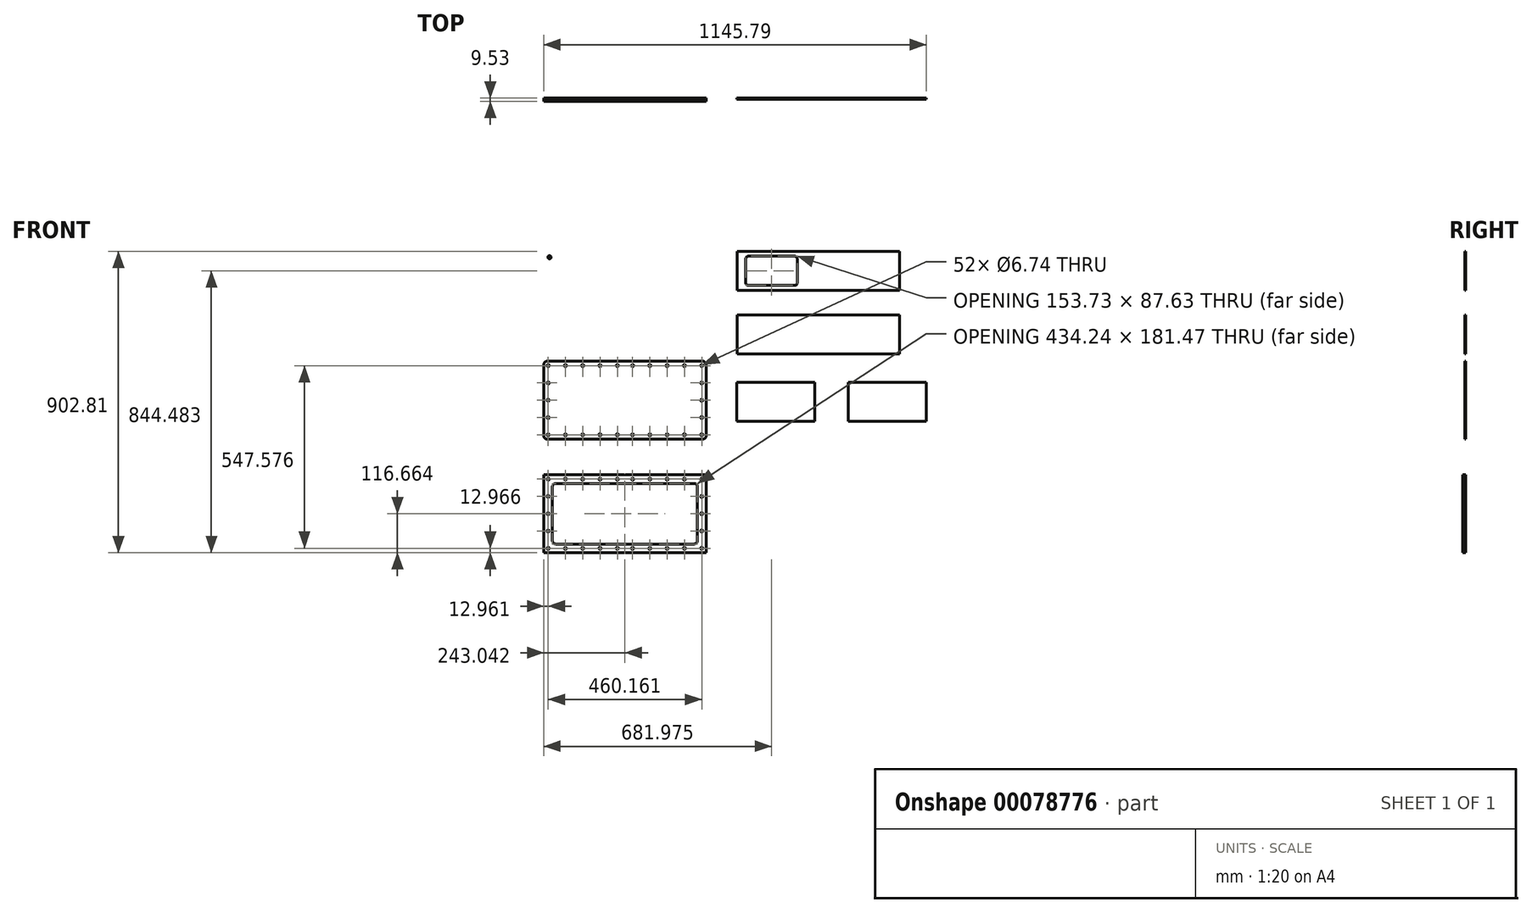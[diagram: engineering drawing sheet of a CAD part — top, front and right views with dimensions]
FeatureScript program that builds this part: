
annotation { "Feature Type Name" : "Feature", "Feature Type Description" : "" }
export const myFeature = defineFeature(function(context is Context, id is Id, definition is map)
    precondition{}
    {
        {
            var Q0;
            Q0=qCreatedBy(makeId("Front.planeOp"),FACE);
            var sketch = newSketch(context, id + "F0", { "sketchPlane" : qUnion([Q0])});
            skLineSegment(sketch, "E0", {"start": v(7.41, 48.73) * mm, "end": v(240.74, 48.73) * mm});
            skLineSegment(sketch, "E1", {"start": v(7.41, 48.73) * mm, "end": v(7.41, -67.93) * mm});
            skLineSegment(sketch, "E2", {"start": v(7.41, -67.93) * mm, "end": v(240.74, -67.93) * mm});
            skLineSegment(sketch, "E3", {"start": v(341.56, 48.73) * mm, "end": v(574.88, 48.73) * mm});
            skLineSegment(sketch, "E4", {"start": v(341.56, -67.93) * mm, "end": v(574.88, -67.93) * mm});
            skLineSegment(sketch, "E5", {"start": v(341.56, 48.73) * mm, "end": v(341.56, -67.93) * mm});
            skLineSegment(sketch, "E6", {"start": v(8.27, 250.62) * mm, "end": v(494.36, 250.62) * mm});
            skLineSegment(sketch, "E7", {"start": v(8.27, 133.96) * mm, "end": v(494.36, 133.96) * mm});
            skLineSegment(sketch, "E8", {"start": v(8.27, 441.5) * mm, "end": v(494.36, 441.5) * mm});
            skLineSegment(sketch, "E9", {"start": v(8.27, 324.83) * mm, "end": v(494.36, 324.83) * mm});
            skLineSegment(sketch, "E10", {"start": v(8.27, 250.62) * mm, "end": v(8.27, 133.96) * mm});
            skLineSegment(sketch, "E11", {"start": v(8.27, 441.5) * mm, "end": v(8.27, 324.83) * mm});
            skCircle(sketch, "E12", {"center": v(-553.9, 424) * mm, "radius": 4.86 * mm});
            skCircle(sketch, "E13", {"center": v(-553.9, 245.77) * mm, "radius": 4.86 * mm});
            skCircle(sketch, "E14", {"center": v(-101.84, 424) * mm, "radius": 4.86 * mm});
            skCircle(sketch, "E15", {"center": v(-131, 245.77) * mm, "radius": 4.86 * mm});
            skCircle(sketch, "E16", {"center": v(-372.43, 430.48) * mm, "radius": 4.86 * mm});
            skCircle(sketch, "E17", {"center": v(-255.77, 430.48) * mm, "radius": 4.86 * mm});
            skCircle(sketch, "E18", {"center": v(-411.31, 239.29) * mm, "radius": 4.86 * mm});
            skCircle(sketch, "E19", {"center": v(-294.65, 239.29) * mm, "radius": 4.86 * mm});
            skLineSegment(sketch, "E20", {"start": v(-570.91, 451.55) * mm, "end": v(-84.83, 451.55) * mm});
            skLineSegment(sketch, "E21", {"start": v(-570.91, 218.23) * mm, "end": v(-84.83, 218.23) * mm});
            skLineSegment(sketch, "E22", {"start": v(-84.83, 451.55) * mm, "end": v(-84.83, 218.23) * mm});
            skLineSegment(sketch, "E23", {"start": v(-570.91, 451.55) * mm, "end": v(-570.91, 218.23) * mm});
            skCircle(sketch, "E24", {"center": v(-515.01, 401.32) * mm, "radius": 4.4 * mm});
            skCircle(sketch, "E25", {"center": v(-515.01, 268.45) * mm, "radius": 4.4 * mm});
            skCircle(sketch, "E26", {"center": v(-369.83, 401.32) * mm, "radius": 4.4 * mm});
            skCircle(sketch, "E27", {"center": v(-369.83, 268.45) * mm, "radius": 4.4 * mm});
            skCircle(sketch, "E28", {"center": v(-285.9, 401.32) * mm, "radius": 4.4 * mm});
            skCircle(sketch, "E29", {"center": v(-285.9, 268.45) * mm, "radius": 4.4 * mm});
            skCircle(sketch, "E30", {"center": v(-140.73, 401.32) * mm, "radius": 4.4 * mm});
            skCircle(sketch, "E31", {"center": v(-140.73, 268.45) * mm, "radius": 4.4 * mm});
            skLineSegment(sketch, "E32", {"start": v(-492.98, 385.76) * mm, "end": v(-391.87, 385.76) * mm});
            skLineSegment(sketch, "E33", {"start": v(-499.46, 290.49) * mm, "end": v(-499.46, 379.28) * mm});
            skLineSegment(sketch, "E34", {"start": v(-492.98, 284) * mm, "end": v(-391.87, 284) * mm});
            skLineSegment(sketch, "E35", {"start": v(-385.39, 290.49) * mm, "end": v(-385.39, 379.28) * mm});
            skLineSegment(sketch, "E36", {"start": v(-270.35, 379.28) * mm, "end": v(-270.35, 290.49) * mm});
            skLineSegment(sketch, "E37", {"start": v(-156.28, 379.28) * mm, "end": v(-156.28, 290.49) * mm});
            skArc(sketch, "E38", {"start": v(-492.98, 385.76) * mm, "mid": v(-497.56, 383.86) * mm, "end": v(-499.46, 379.28) * mm});
            skLineSegment(sketch, "E39", {"start": v(-263.87, 385.76) * mm, "end": v(-162.76, 385.76) * mm});
            skLineSegment(sketch, "E40", {"start": v(-263.87, 284) * mm, "end": v(-162.76, 284) * mm});
            skArc(sketch, "E41", {"start": v(-385.39, 379.28) * mm, "mid": v(-387.29, 383.86) * mm, "end": v(-391.87, 385.76) * mm});
            skArc(sketch, "E42", {"start": v(-391.87, 284) * mm, "mid": v(-387.29, 285.9) * mm, "end": v(-385.39, 290.49) * mm});
            skArc(sketch, "E43", {"start": v(-499.46, 290.49) * mm, "mid": v(-497.56, 285.9) * mm, "end": v(-492.98, 284) * mm});
            skArc(sketch, "E44", {"start": v(-270.35, 290.49) * mm, "mid": v(-268.45, 285.9) * mm, "end": v(-263.87, 284) * mm});
            skArc(sketch, "E45", {"start": v(-263.87, 385.76) * mm, "mid": v(-268.45, 383.86) * mm, "end": v(-270.35, 379.28) * mm});
            skArc(sketch, "E46", {"start": v(-156.28, 379.28) * mm, "mid": v(-158.18, 383.86) * mm, "end": v(-162.76, 385.76) * mm});
            skArc(sketch, "E47", {"start": v(-162.76, 284) * mm, "mid": v(-158.18, 285.9) * mm, "end": v(-156.28, 290.49) * mm});
            skLineSegment(sketch, "E48", {"start": v(-561.19, -121.14) * mm, "end": v(-94.55, -121.14) * mm});
            skLineSegment(sketch, "E49", {"start": v(-561.19, 112.18) * mm, "end": v(-94.55, 112.18) * mm});
            skLineSegment(sketch, "E50", {"start": v(-570.91, 102.46) * mm, "end": v(-570.91, -111.42) * mm});
            skLineSegment(sketch, "E51", {"start": v(-84.83, 102.46) * mm, "end": v(-84.83, -111.42) * mm});
            skCircle(sketch, "E52", {"center": v(-557.95, 99.22) * mm, "radius": 3.37 * mm});
            skCircle(sketch, "E53", {"center": v(-506.1, 99.22) * mm, "radius": 3.37 * mm});
            skCircle(sketch, "E54", {"center": v(-454.25, 99.22) * mm, "radius": 3.37 * mm});
            skCircle(sketch, "E55", {"center": v(-402.4, 99.22) * mm, "radius": 3.37 * mm});
            skCircle(sketch, "E56", {"center": v(-350.55, 99.22) * mm, "radius": 3.37 * mm});
            skCircle(sketch, "E57", {"center": v(-305.18, 99.22) * mm, "radius": 3.37 * mm});
            skCircle(sketch, "E58", {"center": v(-253.33, 99.22) * mm, "radius": 3.37 * mm});
            skCircle(sketch, "E59", {"center": v(-201.49, 99.22) * mm, "radius": 3.37 * mm});
            skCircle(sketch, "E60", {"center": v(-149.64, 99.22) * mm, "radius": 3.37 * mm});
            skCircle(sketch, "E61", {"center": v(-97.79, 99.22) * mm, "radius": 3.37 * mm});
            skCircle(sketch, "E62", {"center": v(-97.79, 47.37) * mm, "radius": 3.37 * mm});
            skCircle(sketch, "E63", {"center": v(-97.79, -4.48) * mm, "radius": 3.37 * mm});
            skCircle(sketch, "E64", {"center": v(-97.79, -56.33) * mm, "radius": 3.37 * mm});
            skCircle(sketch, "E65", {"center": v(-97.79, -108.17) * mm, "radius": 3.37 * mm});
            skCircle(sketch, "E66", {"center": v(-149.64, -108.17) * mm, "radius": 3.37 * mm});
            skCircle(sketch, "E67", {"center": v(-201.49, -108.17) * mm, "radius": 3.37 * mm});
            skCircle(sketch, "E68", {"center": v(-253.33, -108.17) * mm, "radius": 3.37 * mm});
            skCircle(sketch, "E69", {"center": v(-305.18, -108.17) * mm, "radius": 3.37 * mm});
            skCircle(sketch, "E70", {"center": v(-350.55, -108.17) * mm, "radius": 3.37 * mm});
            skCircle(sketch, "E71", {"center": v(-402.4, -108.17) * mm, "radius": 3.37 * mm});
            skCircle(sketch, "E72", {"center": v(-454.25, -108.17) * mm, "radius": 3.37 * mm});
            skCircle(sketch, "E73", {"center": v(-506.1, -108.17) * mm, "radius": 3.37 * mm});
            skCircle(sketch, "E74", {"center": v(-557.95, -108.17) * mm, "radius": 3.37 * mm});
            skCircle(sketch, "E75", {"center": v(-557.95, -56.33) * mm, "radius": 3.37 * mm});
            skCircle(sketch, "E76", {"center": v(-557.95, -4.48) * mm, "radius": 3.37 * mm});
            skCircle(sketch, "E77", {"center": v(-557.95, 47.37) * mm, "radius": 3.37 * mm});
            skArc(sketch, "E78", {"start": v(-84.83, 102.46) * mm, "mid": v(-87.67, 109.34) * mm, "end": v(-94.55, 112.18) * mm});
            skArc(sketch, "E79", {"start": v(-94.55, -121.14) * mm, "mid": v(-87.67, -118.29) * mm, "end": v(-84.83, -111.42) * mm});
            skArc(sketch, "E80", {"start": v(-570.91, -111.42) * mm, "mid": v(-568.06, -118.29) * mm, "end": v(-561.19, -121.14) * mm});
            skArc(sketch, "E81", {"start": v(-561.19, 112.18) * mm, "mid": v(-568.06, 109.34) * mm, "end": v(-570.91, 102.46) * mm});
            skLineSegment(sketch, "E82", {"start": v(-570.91, -461.32) * mm, "end": v(-84.83, -461.32) * mm});
            skLineSegment(sketch, "E83", {"start": v(-570.91, -228) * mm, "end": v(-84.83, -228) * mm});
            skLineSegment(sketch, "E84", {"start": v(-570.91, -228) * mm, "end": v(-570.91, -461.32) * mm});
            skLineSegment(sketch, "E85", {"start": v(-84.83, -228) * mm, "end": v(-84.83, -461.32) * mm});
            skCircle(sketch, "E86", {"center": v(-557.95, -240.96) * mm, "radius": 3.37 * mm});
            skCircle(sketch, "E87", {"center": v(-506.1, -240.96) * mm, "radius": 3.37 * mm});
            skCircle(sketch, "E88", {"center": v(-454.25, -240.96) * mm, "radius": 3.37 * mm});
            skCircle(sketch, "E89", {"center": v(-402.4, -240.96) * mm, "radius": 3.37 * mm});
            skCircle(sketch, "E90", {"center": v(-350.55, -240.96) * mm, "radius": 3.37 * mm});
            skCircle(sketch, "E91", {"center": v(-305.18, -240.96) * mm, "radius": 3.37 * mm});
            skCircle(sketch, "E92", {"center": v(-253.33, -240.96) * mm, "radius": 3.37 * mm});
            skCircle(sketch, "E93", {"center": v(-201.49, -240.96) * mm, "radius": 3.37 * mm});
            skCircle(sketch, "E94", {"center": v(-149.64, -240.96) * mm, "radius": 3.37 * mm});
            skCircle(sketch, "E95", {"center": v(-97.79, -240.96) * mm, "radius": 3.37 * mm});
            skCircle(sketch, "E96", {"center": v(-97.79, -292.8) * mm, "radius": 3.37 * mm});
            skCircle(sketch, "E97", {"center": v(-97.79, -344.66) * mm, "radius": 3.37 * mm});
            skCircle(sketch, "E98", {"center": v(-97.79, -396.5) * mm, "radius": 3.37 * mm});
            skCircle(sketch, "E99", {"center": v(-97.79, -448.35) * mm, "radius": 3.37 * mm});
            skCircle(sketch, "E100", {"center": v(-149.64, -448.35) * mm, "radius": 3.37 * mm});
            skCircle(sketch, "E101", {"center": v(-201.49, -448.35) * mm, "radius": 3.37 * mm});
            skCircle(sketch, "E102", {"center": v(-253.33, -448.35) * mm, "radius": 3.37 * mm});
            skCircle(sketch, "E103", {"center": v(-305.18, -448.35) * mm, "radius": 3.37 * mm});
            skCircle(sketch, "E104", {"center": v(-350.55, -448.35) * mm, "radius": 3.37 * mm});
            skCircle(sketch, "E105", {"center": v(-402.4, -448.35) * mm, "radius": 3.37 * mm});
            skCircle(sketch, "E106", {"center": v(-454.25, -448.35) * mm, "radius": 3.37 * mm});
            skCircle(sketch, "E107", {"center": v(-506.1, -448.35) * mm, "radius": 3.37 * mm});
            skCircle(sketch, "E108", {"center": v(-557.95, -448.35) * mm, "radius": 3.37 * mm});
            skCircle(sketch, "E109", {"center": v(-557.95, -396.5) * mm, "radius": 3.37 * mm});
            skCircle(sketch, "E110", {"center": v(-557.95, -344.66) * mm, "radius": 3.37 * mm});
            skCircle(sketch, "E111", {"center": v(-557.95, -292.8) * mm, "radius": 3.37 * mm});
            skLineSegment(sketch, "E112", {"start": v(-535.26, -253.92) * mm, "end": v(-120.47, -253.92) * mm});
            skLineSegment(sketch, "E113", {"start": v(-535.26, -435.4) * mm, "end": v(-120.47, -435.4) * mm});
            skLineSegment(sketch, "E114", {"start": v(-544.99, -263.64) * mm, "end": v(-544.99, -425.67) * mm});
            skLineSegment(sketch, "E115", {"start": v(-110.75, -263.64) * mm, "end": v(-110.75, -425.67) * mm});
            skArc(sketch, "E116", {"start": v(-535.26, -253.92) * mm, "mid": v(-542.14, -256.77) * mm, "end": v(-544.99, -263.64) * mm});
            skArc(sketch, "E117", {"start": v(-544.99, -425.67) * mm, "mid": v(-542.14, -432.54) * mm, "end": v(-535.26, -435.4) * mm});
            skArc(sketch, "E118", {"start": v(-120.47, -435.4) * mm, "mid": v(-113.6, -432.54) * mm, "end": v(-110.75, -425.67) * mm});
            skArc(sketch, "E119", {"start": v(-110.75, -263.64) * mm, "mid": v(-113.6, -256.77) * mm, "end": v(-120.47, -253.92) * mm});
            skLineSegment(sketch, "E120", {"start": v(494.36, 441.5) * mm, "end": v(494.36, 324.83) * mm});
            skLineSegment(sketch, "E121", {"start": v(494.36, 250.62) * mm, "end": v(494.36, 133.96) * mm});
            skLineSegment(sketch, "E122", {"start": v(240.74, 48.73) * mm, "end": v(240.74, -67.93) * mm});
            skLineSegment(sketch, "E123", {"start": v(574.88, 48.73) * mm, "end": v(574.88, -67.93) * mm});
            skLineSegment(sketch, "E124", {"start": v(34.2, 420.5) * mm, "end": v(34.2, 345.83) * mm});
            skLineSegment(sketch, "E125", {"start": v(187.93, 420.5) * mm, "end": v(187.93, 345.83) * mm});
            skLineSegment(sketch, "E126", {"start": v(40.68, 339.35) * mm, "end": v(181.45, 339.35) * mm});
            skLineSegment(sketch, "E127", {"start": v(40.68, 426.98) * mm, "end": v(181.45, 426.98) * mm});
            skArc(sketch, "E128", {"start": v(40.68, 426.98) * mm, "mid": v(36.1, 425.08) * mm, "end": v(34.2, 420.5) * mm});
            skArc(sketch, "E129", {"start": v(187.93, 420.5) * mm, "mid": v(186.03, 425.08) * mm, "end": v(181.45, 426.98) * mm});
            skArc(sketch, "E130", {"start": v(181.45, 339.35) * mm, "mid": v(186.03, 341.25) * mm, "end": v(187.93, 345.83) * mm});
            skArc(sketch, "E131", {"start": v(34.2, 345.83) * mm, "mid": v(36.1, 341.25) * mm, "end": v(40.68, 339.35) * mm});
            skSolve(sketch);
        }
        {
            var Q0;
            Q0=makeQuery(id+"F0.imprint","IMPRINT",FACE,{"disambiguationData":[TD([[makeQuery(id+"F0.imprint","IMPRINT",EDGE,{"derivedFrom":sQuery(id+"F0.wireOp",EDGE,"E12")}),1.0]])]});
            var Q1;
            Q1=makeQuery(id+"F0.imprint","IMPRINT",FACE,{"disambiguationData":[TD([[makeQuery(id+"F0.imprint","IMPRINT",EDGE,{"derivedFrom":sQuery(id+"F0.wireOp",EDGE,"E8")}),-1.0]])]});
            var Q2;
            Q2=makeQuery(id+"F0.imprint","IMPRINT",FACE,{"disambiguationData":[TD([[makeQuery(id+"F0.imprint","IMPRINT",EDGE,{"derivedFrom":sQuery(id+"F0.wireOp",EDGE,"E6")}),-1.0]])]});
            var Q3;
            Q3=makeQuery(id+"F0.imprint","IMPRINT",FACE,{"disambiguationData":[TD([[makeQuery(id+"F0.imprint","IMPRINT",EDGE,{"derivedFrom":sQuery(id+"F0.wireOp",EDGE,"E3")}),-1.0]])]});
            var Q4;
            Q4=makeQuery(id+"F0.imprint","IMPRINT",FACE,{"disambiguationData":[TD([[makeQuery(id+"F0.imprint","IMPRINT",EDGE,{"derivedFrom":sQuery(id+"F0.wireOp",EDGE,"E0")}),-1.0]])]});
            var Q5;
            Q5=makeQuery(id+"F0.imprint","IMPRINT",FACE,{"disambiguationData":[TD([[makeQuery(id+"F0.imprint","IMPRINT",EDGE,{"derivedFrom":sQuery(id+"F0.wireOp",EDGE,"E48")}),1.0]])]});
            extrude(context, id + "F1", {"entities" : qUnion([Q0, Q1, Q2, Q3, Q4, Q5]), "depth" : 3.17 * mm});
        }
        {
            var Q0;
            Q0=makeQuery(id+"F0.imprint","IMPRINT",FACE,{"disambiguationData":[TD([[makeQuery(id+"F0.imprint","IMPRINT",EDGE,{"derivedFrom":sQuery(id+"F0.wireOp",EDGE,"E82")}),1.0]])]});
            extrude(context, id + "F2", {"entities" : qUnion([Q0]), "depth" : 9.52 * mm});
        }
    });
